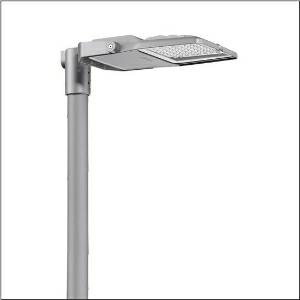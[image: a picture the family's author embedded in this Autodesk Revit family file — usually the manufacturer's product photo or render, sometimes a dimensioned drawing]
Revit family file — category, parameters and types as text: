
# Revit family: floodlight_fl_21_mini___pl33t_5xa7776d2f3a_276e
name_source: partatom
category: Lighting Fixtures
units: mm (PartAtom-declared; Revit-internal decimal feet)

## family parameters
Cut with Voids When Loaded = No
Host = Face
Light Source = No
Part Type = Normal
Room Calculation Point = No
Round Connector Dimension = Use Diameter
Shared = No

## types (1)
- --- (1 x LED, 17630 lm, 142.9 W, 3000K)
    Apparent Load = 143 VA
    CIE Flux Codes = 26 75 99 100 100
    Color Rendering = 70
    Color Temperature = 3000K
    Default Elevation = 1800 mm
    Description = Floodlight FL 21 mini, floodlight, primary light control with lens, of PMMA, primary optical cover: protective disc, of toughened safety glass, transparent, light distribution: PL33T, light emission: direct distribution, installation type: surface-mounted, LED, High Power LED, rated luminous flux: 17.630lm, luminous efficacy: 123lm/W, light colour: 730, colour temperature: 3000K, control gear: Smart Interface (Zhaga), control: flexible luminous flux parameterisation, time-dependent luminous flux control, constant luminous flux control, overheat protection, pre-setting: logarithmic dimming characteristic, with terminal, 6-pole, mains connection: 220..240V, AC, 50/60Hz, start of lifetime: 143W, end of service life: 151W, reduction: 63W, luminaire housing, of diecast aluminium, powder-coated, Siteco® metallic grey (DB 702S), corrosivity category C5 mid according to DIN EN ISO 12944, suitable for swimming pools, chlorine-resistant, sealing non-destructively replaceable, please order mast flange separately, mast bracket, of steel, galvanised, powder-coated, Siteco® metallic grey (DB 702S), Smart Interface below and above, protection rating (complete): IP66, insulation class (complete): insulation class II (safety insulation), certification: CE, ENEC, VDE, protection symbol: D, impact resistance: IK08, permissible operating ambient temperature: -40..+40°C, permissible operating ambient temperature for outdoor applications: -40..+50°C, standard: DIN EN 12944, LABS conformity tested according to VDMA 24364:2018-05, packaging unit: 1 piece

Light Distribution: PL33T
    Height = 70 mm
    Lamp = 1 x LED
    Lamp Light Flux = 17630 lm
    Lamp Power = 142.9 W
    Lamp count = 1
    Length = 485 mm
    Luminous efficacy = 123 lm/W
    Manufacturer = Siteco
    ModVariant = No
    Model = 5XA7776D2F3A
    Number of Poles = 1
    OnlyDefault = Yes
    Power Factor = 1
    Product Name = Floodlight FL 21 mini | PL33T
    Product group = floodlight | pylon annexe
    ProductGroupID = 6200
    Protection Class = Protection class II
    Protection Degree = IP 66
    RLX_Detail_Level = 1
    RLX_Emergency_Light_Flux = 0 lm
    RLX_Emergency_Type = 0
    RLX_Emergency_Type_DB = No
    RlxData = <blob elided: 101165 chars, md5=36604541>
    Socket = socket
    Standby Power = 0 W
    System Light Flux = 17630 lm
    System Power = 143 W
    Type Comments = factory setting: luminous flux: 100 % | dim-lin: 254 | 730 mA
    Type Image = l_1007125.jpg
    URL = http://relux.com
    VarID = @adj_148334
    Voltage = 0 V
    Weight = 0.00 kg
    Width = 337 mm

## geometry (parser evidence)
native form markers: Blend x4, Sweep x13
no freeform markers — native parametric forms only
